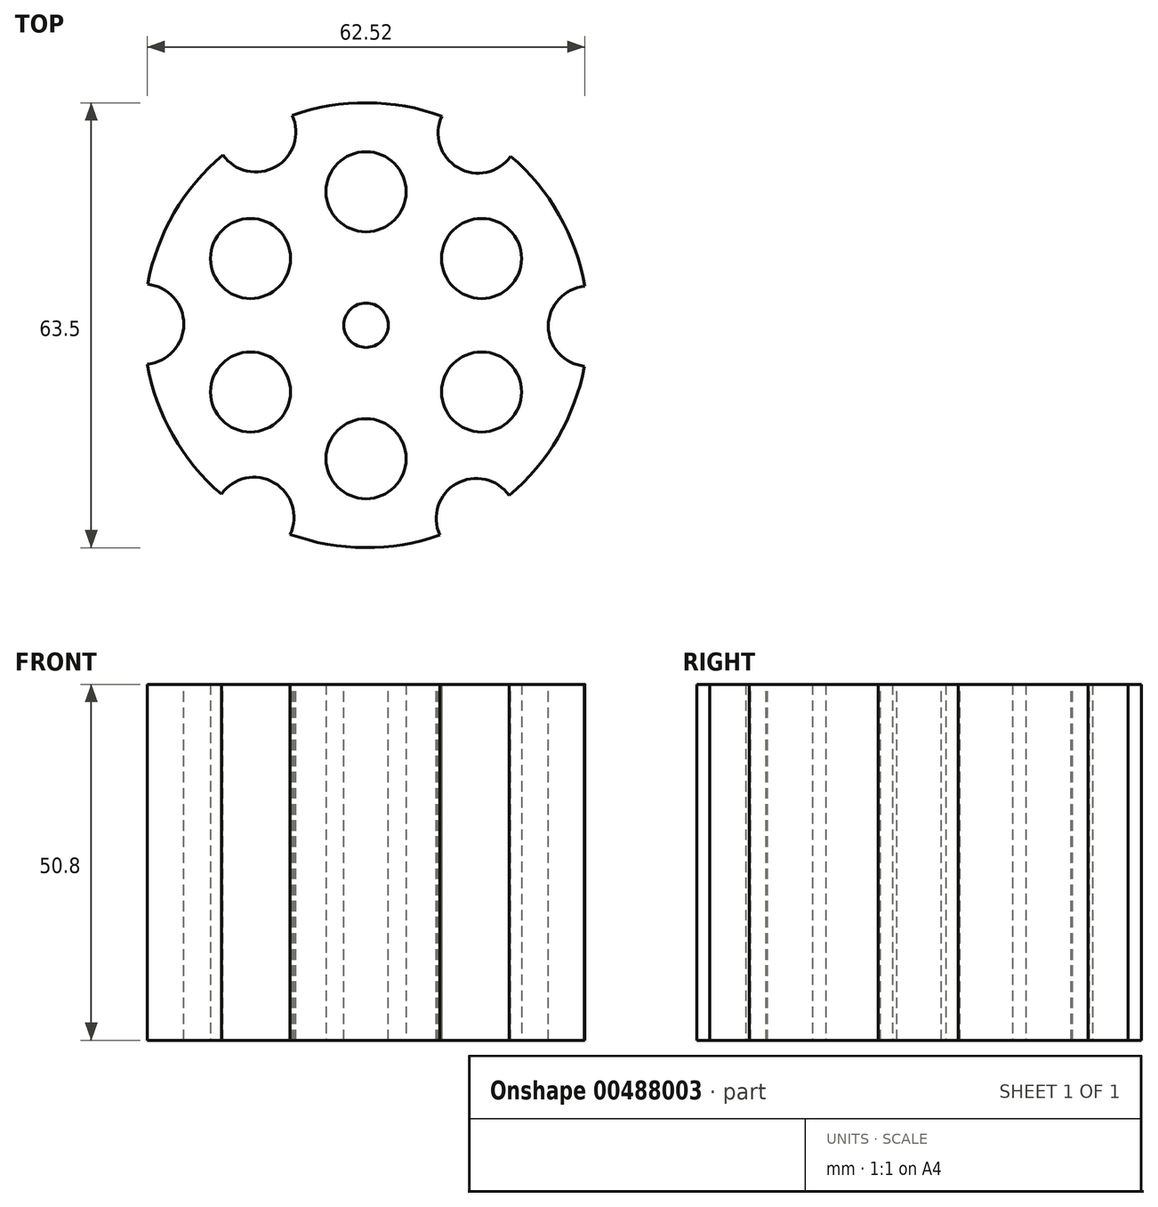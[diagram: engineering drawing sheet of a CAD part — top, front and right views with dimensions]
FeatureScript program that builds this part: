
annotation { "Feature Type Name" : "Feature", "Feature Type Description" : "" }
export const myFeature = defineFeature(function(context is Context, id is Id, definition is map)
    precondition{}
    {
        {
            var Q0;
            Q0=qCreatedBy(makeId("Top.planeOp"),FACE);
            var sketch = newSketch(context, id + "F0", { "sketchPlane" : qUnion([Q0])});
            skCircle(sketch, "E0", {"center": v(0, 0) * mm, "radius": 31.75 * mm});
            skLineSegment(sketch, "E1", {"start": v(0, 0) * mm, "end": v(0, 19.05) * mm});
            skCircle(sketch, "E2", {"center": v(0, 19.05) * mm, "radius": 5.72 * mm});
            skCircle(sketch, "E3.1.0", {"center": v(-16.5, 9.53) * mm, "radius": 5.72 * mm});
            skCircle(sketch, "E3.2.0", {"center": v(-16.5, -9.52) * mm, "radius": 5.72 * mm});
            skCircle(sketch, "E3.3.0", {"center": v(0, -19.05) * mm, "radius": 5.72 * mm});
            skCircle(sketch, "E3.4.0", {"center": v(16.5, -9.53) * mm, "radius": 5.72 * mm});
            skCircle(sketch, "E3.5.0", {"center": v(16.5, 9.53) * mm, "radius": 5.72 * mm});
            skSolve(sketch);
        }
        {
            var Q0;
            Q0=makeQuery(id+"F0.imprint","IMPRINT",FACE,{"disambiguationData":[TD([[makeQuery(id+"F0.imprint","IMPRINT",EDGE,{"derivedFrom":sQuery(id+"F0.wireOp",EDGE,"E0")}),1.0]])]});
            extrude(context, id + "F1", {"entities" : qUnion([Q0]), "depth" : 50.8 * mm});
        }
        {
            var Q0;
            Q0=makeQuery(id+"F1.opExtrude","CAP_FACE",FACE,{"disambiguationData":[OSD([sQuery(id+"F0.wireOp",EDGE,"E0"),sQuery(id+"F0.wireOp",EDGE,"E2"),sQuery(id+"F0.wireOp",EDGE,"E3.1.0"),sQuery(id+"F0.wireOp",EDGE,"E3.2.0"),sQuery(id+"F0.wireOp",EDGE,"E3.3.0"),sQuery(id+"F0.wireOp",EDGE,"E3.4.0"),sQuery(id+"F0.wireOp",EDGE,"E3.5.0")])],"isStart":false});
            var sketch = newSketch(context, id + "F2", { "sketchPlane" : qUnion([Q0])});
            skLineSegment(sketch, "E4", {"start": v(0, 0) * mm, "end": v(-15.74, 27.57) * mm});
            skLineSegment(sketch, "E5", {"start": v(-15.74, 27.57) * mm, "end": v(-31.75, 0) * mm});
            skLineSegment(sketch, "E6", {"start": v(-31.75, 0) * mm, "end": v(0, 0) * mm});
            skCircle(sketch, "E7", {"center": v(-15.74, 27.57) * mm, "radius": 5.72 * mm});
            skCircle(sketch, "E8.1.0", {"center": v(-31.75, 0.15) * mm, "radius": 5.72 * mm});
            skCircle(sketch, "E8.2.0", {"center": v(-16, -27.42) * mm, "radius": 5.72 * mm});
            skCircle(sketch, "E8.3.0", {"center": v(15.74, -27.57) * mm, "radius": 5.72 * mm});
            skCircle(sketch, "E8.4.0", {"center": v(31.75, -0.15) * mm, "radius": 5.72 * mm});
            skCircle(sketch, "E8.5.0", {"center": v(16, 27.42) * mm, "radius": 5.72 * mm});
            skPoint(sketch, "E8.center", {"position": v(0, 0) * mm});
            skSolve(sketch);
        }
        {
            var Q0;
            {var subQ0=sQuery(id+"F2.wireOp",EDGE,"E8.5.0");var subQ1=makeQuery(id+"F1.opExtrude","CAP_EDGE",EDGE,{"disambiguationData":[OSD([sQuery(id+"F0.wireOp",EDGE,"E0")])],"isStart":false});var subQ2=makeQuery(id+"F2.imprint","INTERSECT",VERTEX,{"disambiguationData":[OD(0.0)],"derivedFrom":[subQ1,subQ0]});Q0=makeQuery(id+"F2.imprint","IMPRINT",FACE,{"disambiguationData":[TD([[makeQuery(id+"F2.imprint","IMPRINT",EDGE,{"disambiguationData":[TD([[subQ2,-1.0]])],"derivedFrom":subQ0}),1.0]])]});}
            var Q1;
            {var subQ0=sQuery(id+"F2.wireOp",EDGE,"E8.5.0");var subQ1=makeQuery(id+"F1.opExtrude","CAP_EDGE",EDGE,{"disambiguationData":[OSD([sQuery(id+"F0.wireOp",EDGE,"E0")])],"isStart":false});var subQ2=makeQuery(id+"F2.imprint","INTERSECT",VERTEX,{"disambiguationData":[OD(0.0)],"derivedFrom":[subQ1,subQ0]});Q1=makeQuery(id+"F2.imprint","IMPRINT",FACE,{"disambiguationData":[TD([[makeQuery(id+"F2.imprint","IMPRINT",EDGE,{"disambiguationData":[TD([[subQ2,1.0]])],"derivedFrom":subQ0}),1.0]])]});}
            var Q2;
            {var subQ0=sQuery(id+"F2.wireOp",EDGE,"E4");var subQ3=sQuery(id+"F2.wireOp",EDGE,"E7");var subQ4=makeQuery(id+"F2.imprint","INTERSECT",VERTEX,{"derivedFrom":[subQ0,subQ3]});Q2=makeQuery(id+"F2.imprint","IMPRINT",FACE,{"disambiguationData":[TD([[makeQuery(id+"F2.imprint","IMPRINT",EDGE,{"disambiguationData":[TD([[subQ4,-1.0]])],"derivedFrom":subQ3}),1.0]])]});}
            var Q3;
            {var subQ1=sQuery(id+"F2.wireOp",EDGE,"E4");var subQ3=sQuery(id+"F2.wireOp",EDGE,"E7");var subQ4=makeQuery(id+"F2.imprint","INTERSECT",VERTEX,{"derivedFrom":[subQ1,subQ3]});Q3=makeQuery(id+"F2.imprint","IMPRINT",FACE,{"disambiguationData":[TD([[makeQuery(id+"F2.imprint","IMPRINT",EDGE,{"disambiguationData":[TD([[subQ4,1.0]])],"derivedFrom":subQ3}),1.0]])]});}
            var Q4;
            {var subQ0=sQuery(id+"F2.wireOp",EDGE,"E5");var subQ3=sQuery(id+"F2.wireOp",EDGE,"E7");var subQ4=makeQuery(id+"F2.imprint","INTERSECT",VERTEX,{"derivedFrom":[subQ0,subQ3]});Q4=makeQuery(id+"F2.imprint","IMPRINT",FACE,{"disambiguationData":[TD([[makeQuery(id+"F2.imprint","IMPRINT",EDGE,{"disambiguationData":[TD([[subQ4,1.0]])],"derivedFrom":subQ3}),1.0]])]});}
            var Q5;
            {var subQ1=sQuery(id+"F2.wireOp",EDGE,"E5");var subQ3=sQuery(id+"F2.wireOp",EDGE,"E8.1.0");var subQ4=makeQuery(id+"F2.imprint","INTERSECT",VERTEX,{"derivedFrom":[subQ1,subQ3]});Q5=makeQuery(id+"F2.imprint","IMPRINT",FACE,{"disambiguationData":[TD([[makeQuery(id+"F2.imprint","IMPRINT",EDGE,{"disambiguationData":[TD([[subQ4,1.0]])],"derivedFrom":subQ3}),1.0]])]});}
            var Q6;
            {var subQ0=sQuery(id+"F2.wireOp",EDGE,"E6");var subQ3=sQuery(id+"F2.wireOp",EDGE,"E8.1.0");var subQ4=makeQuery(id+"F2.imprint","INTERSECT",VERTEX,{"derivedFrom":[subQ0,subQ3]});Q6=makeQuery(id+"F2.imprint","IMPRINT",FACE,{"disambiguationData":[TD([[makeQuery(id+"F2.imprint","IMPRINT",EDGE,{"disambiguationData":[TD([[subQ4,1.0]])],"derivedFrom":subQ3}),1.0]])]});}
            var Q7;
            {var subQ0=sQuery(id+"F2.wireOp",EDGE,"E5");var subQ3=sQuery(id+"F2.wireOp",EDGE,"E8.1.0");var subQ4=makeQuery(id+"F2.imprint","INTERSECT",VERTEX,{"derivedFrom":[subQ0,subQ3]});Q7=makeQuery(id+"F2.imprint","IMPRINT",FACE,{"disambiguationData":[TD([[makeQuery(id+"F2.imprint","IMPRINT",EDGE,{"disambiguationData":[TD([[subQ4,-1.0]])],"derivedFrom":subQ3}),1.0]])]});}
            var Q8;
            {var subQ0=sQuery(id+"F2.wireOp",EDGE,"E8.2.0");var subQ1=makeQuery(id+"F1.opExtrude","CAP_EDGE",EDGE,{"disambiguationData":[OSD([sQuery(id+"F0.wireOp",EDGE,"E0")])],"isStart":false});var subQ2=makeQuery(id+"F2.imprint","INTERSECT",VERTEX,{"disambiguationData":[OD(0.0)],"derivedFrom":[subQ1,subQ0]});Q8=makeQuery(id+"F2.imprint","IMPRINT",FACE,{"disambiguationData":[TD([[makeQuery(id+"F2.imprint","IMPRINT",EDGE,{"disambiguationData":[TD([[subQ2,1.0]])],"derivedFrom":subQ0}),1.0]])]});}
            var Q9;
            {var subQ0=sQuery(id+"F2.wireOp",EDGE,"E8.3.0");var subQ1=makeQuery(id+"F1.opExtrude","CAP_EDGE",EDGE,{"disambiguationData":[OSD([sQuery(id+"F0.wireOp",EDGE,"E0")])],"isStart":false});var subQ2=makeQuery(id+"F2.imprint","INTERSECT",VERTEX,{"disambiguationData":[OD(0.0)],"derivedFrom":[subQ1,subQ0]});Q9=makeQuery(id+"F2.imprint","IMPRINT",FACE,{"disambiguationData":[TD([[makeQuery(id+"F2.imprint","IMPRINT",EDGE,{"disambiguationData":[TD([[subQ2,1.0]])],"derivedFrom":subQ0}),1.0]])]});}
            var Q10;
            {var subQ0=sQuery(id+"F2.wireOp",EDGE,"E8.4.0");var subQ1=makeQuery(id+"F1.opExtrude","CAP_EDGE",EDGE,{"disambiguationData":[OSD([sQuery(id+"F0.wireOp",EDGE,"E0")])],"isStart":false});var subQ2=makeQuery(id+"F2.imprint","INTERSECT",VERTEX,{"disambiguationData":[OD(0.0)],"derivedFrom":[subQ1,subQ0]});Q10=makeQuery(id+"F2.imprint","IMPRINT",FACE,{"disambiguationData":[TD([[makeQuery(id+"F2.imprint","IMPRINT",EDGE,{"disambiguationData":[TD([[subQ2,-1.0]])],"derivedFrom":subQ0}),1.0]])]});}
            extrude(context, id + "F3", {"entities" : qUnion([Q0, Q1, Q2, Q3, Q4, Q5, Q6, Q7, Q8, Q9, Q10]), "operationType" : NewBodyOperationType.REMOVE, "oppositeDirection" : true, "depth" : 76.2 * mm});
        }
        {
            var Q0;
            Q0=makeQuery(id+"F1.opExtrude","CAP_FACE",FACE,{"disambiguationData":[OSD([sQuery(id+"F0.wireOp",EDGE,"E0"),sQuery(id+"F0.wireOp",EDGE,"E2"),sQuery(id+"F0.wireOp",EDGE,"E3.1.0"),sQuery(id+"F0.wireOp",EDGE,"E3.2.0"),sQuery(id+"F0.wireOp",EDGE,"E3.3.0"),sQuery(id+"F0.wireOp",EDGE,"E3.4.0"),sQuery(id+"F0.wireOp",EDGE,"E3.5.0")])],"isStart":false});
            var sketch = newSketch(context, id + "F4", { "sketchPlane" : qUnion([Q0])});
            skCircle(sketch, "E9", {"center": v(0, 0) * mm, "radius": 3.18 * mm});
            skSolve(sketch);
        }
        {
            var Q0;
            Q0=makeQuery(id+"F4.imprint","IMPRINT",FACE,{"disambiguationData":[TD([[makeQuery(id+"F4.imprint","IMPRINT",EDGE,{"derivedFrom":sQuery(id+"F4.wireOp",EDGE,"E9")}),1.0]])]});
            extrude(context, id + "F5", {"entities" : qUnion([Q0]), "operationType" : NewBodyOperationType.REMOVE, "oppositeDirection" : true, "depth" : 76.2 * mm});
        }
    });
